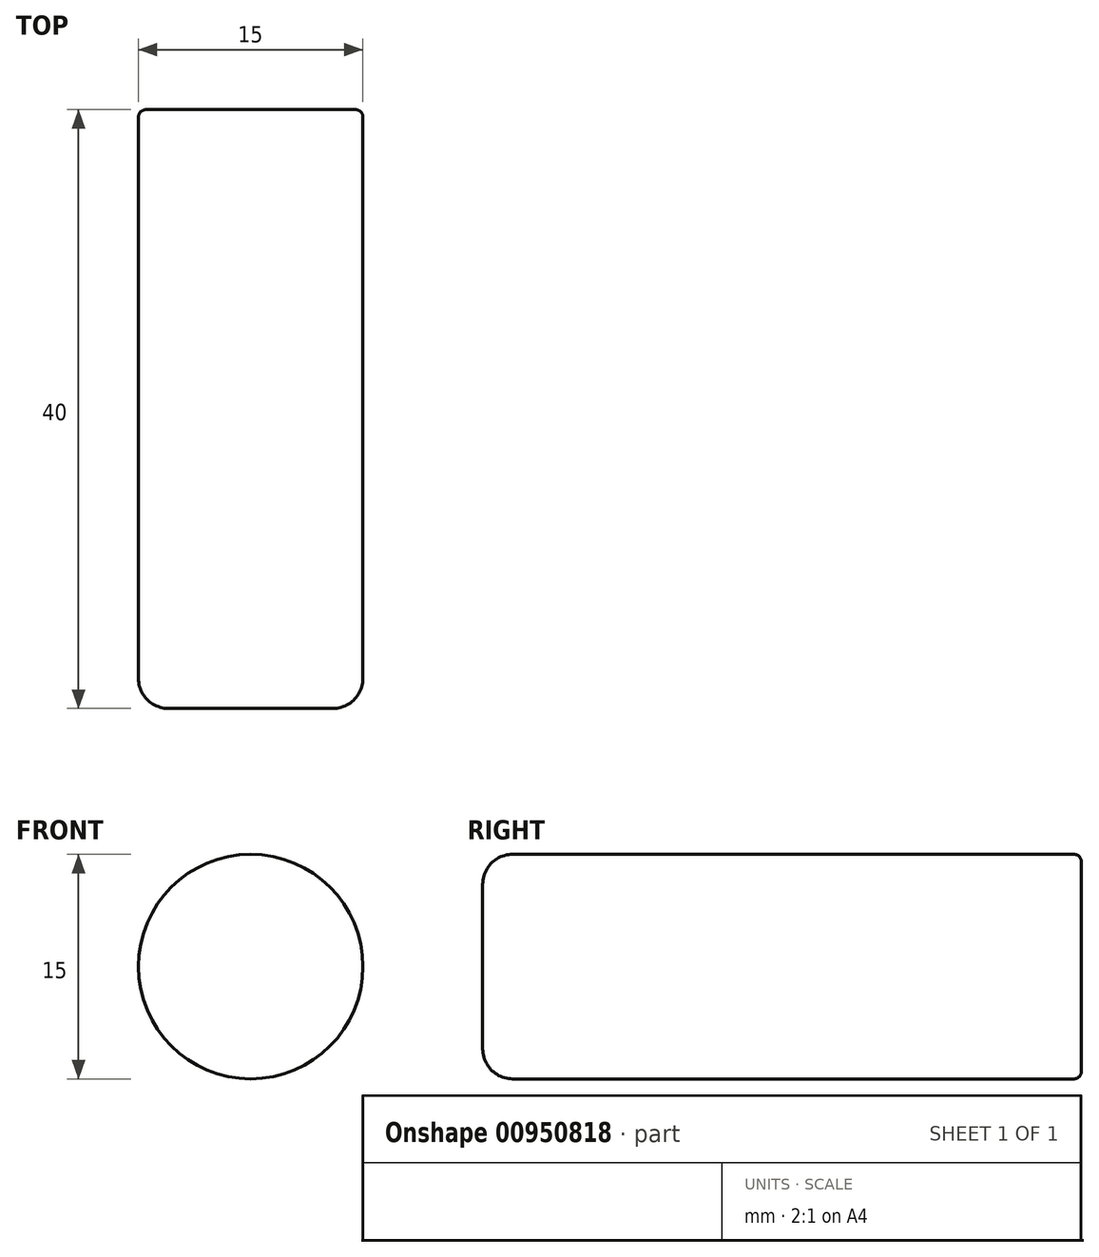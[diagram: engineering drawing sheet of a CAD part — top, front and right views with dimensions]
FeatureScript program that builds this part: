
annotation { "Feature Type Name" : "Feature", "Feature Type Description" : "" }
export const myFeature = defineFeature(function(context is Context, id is Id, definition is map)
    precondition{}
    {
        {
            var Q0;
            Q0=qCreatedBy(makeId("Front.planeOp"),FACE);
            var sketch = newSketch(context, id + "F0", { "sketchPlane" : qUnion([Q0])});
            skCircle(sketch, "E0", {"center": v(0, 0) * mm, "radius": 7.5 * mm});
            skSolve(sketch);
        }
        {
            var Q0;
            Q0=qSketchRegion(id+"F0",true);
            extrude(context, id + "F1", {"entities" : qUnion([Q0]), "depth" : 40 * mm, "offsetDistance" : 25.4 * mm});
        }
        {
            var Q0;
            Q0=makeQuery(id+"F1.opExtrude","CAP_EDGE",EDGE,{"disambiguationData":[OSD([sQuery(id+"F0.wireOp",EDGE,"E0")])],"isStart":false});
            fillet(context, id + "F2", {"entities" : qUnion([Q0]), "radius" : 2 * mm, "tangentPropagation" : true, "allowEdgeOverflow" : false});
        }
        {
            var Q0;
            Q0=makeQuery(id+"F1.opExtrude","CAP_EDGE",EDGE,{"disambiguationData":[OSD([sQuery(id+"F0.wireOp",EDGE,"E0")])],"isStart":true});
            fillet(context, id + "F3", {"entities" : qUnion([Q0]), "radius" : 0.5 * mm, "tangentPropagation" : true, "allowEdgeOverflow" : false});
        }
    });
